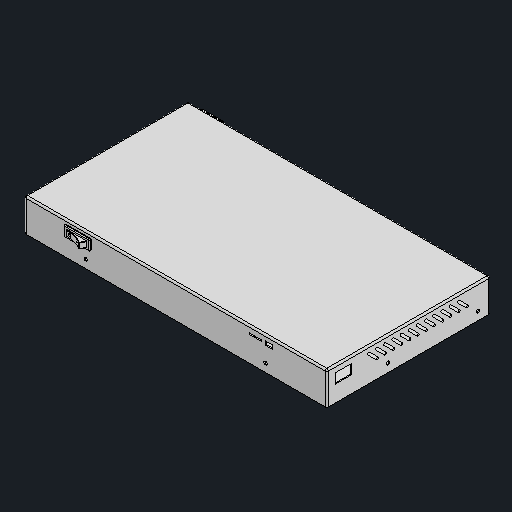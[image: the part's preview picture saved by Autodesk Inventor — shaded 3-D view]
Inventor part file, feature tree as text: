
AUTODESK INVENTOR PART (.ipt)
format: ipt  version: 2024.2 (Build 282272000, 272)  size: 714,240 bytes
history: native  units: mm
features: other x15, chamfer x1
ambient origin geometry x8: Origin, YZ Plane, XZ Plane, XY Plane, X Axis, Y Axis, Z Axis, Center Point
bodies: Body1 (feature_tree), Body2 (feature_tree), Body3 (feature_tree), Body4 (feature_tree), Body5 (feature_tree), Body6 (feature_tree), Body7 (feature_tree), Body8 (feature_tree)
feature tree (16):
  other  "솔리드1"
  other  "솔리드2"
  other  "솔리드3"
  other  "솔리드4"
  other  "솔리드5"
  other  "솔리드6"
  other  "솔리드7"
  other  "솔리드8"
  other  "Wrap2"
  other  "Cut-Extrude6[2]"
  other  "Cut-Extrude6[3]"
  chamfer  "Chamfer2"  [1 undecoded]
  other  "Boss-Extrude13"
  other  "Cut-Extrude9"
  other  "Boss-Extrude17"
  other  "Cut-Extrude11"
note: 1 required parameter value undecoded (feature->parameter linkage not recoverable at this tier; creation-order binding heuristic only, values carry confidence <= 0.55)
